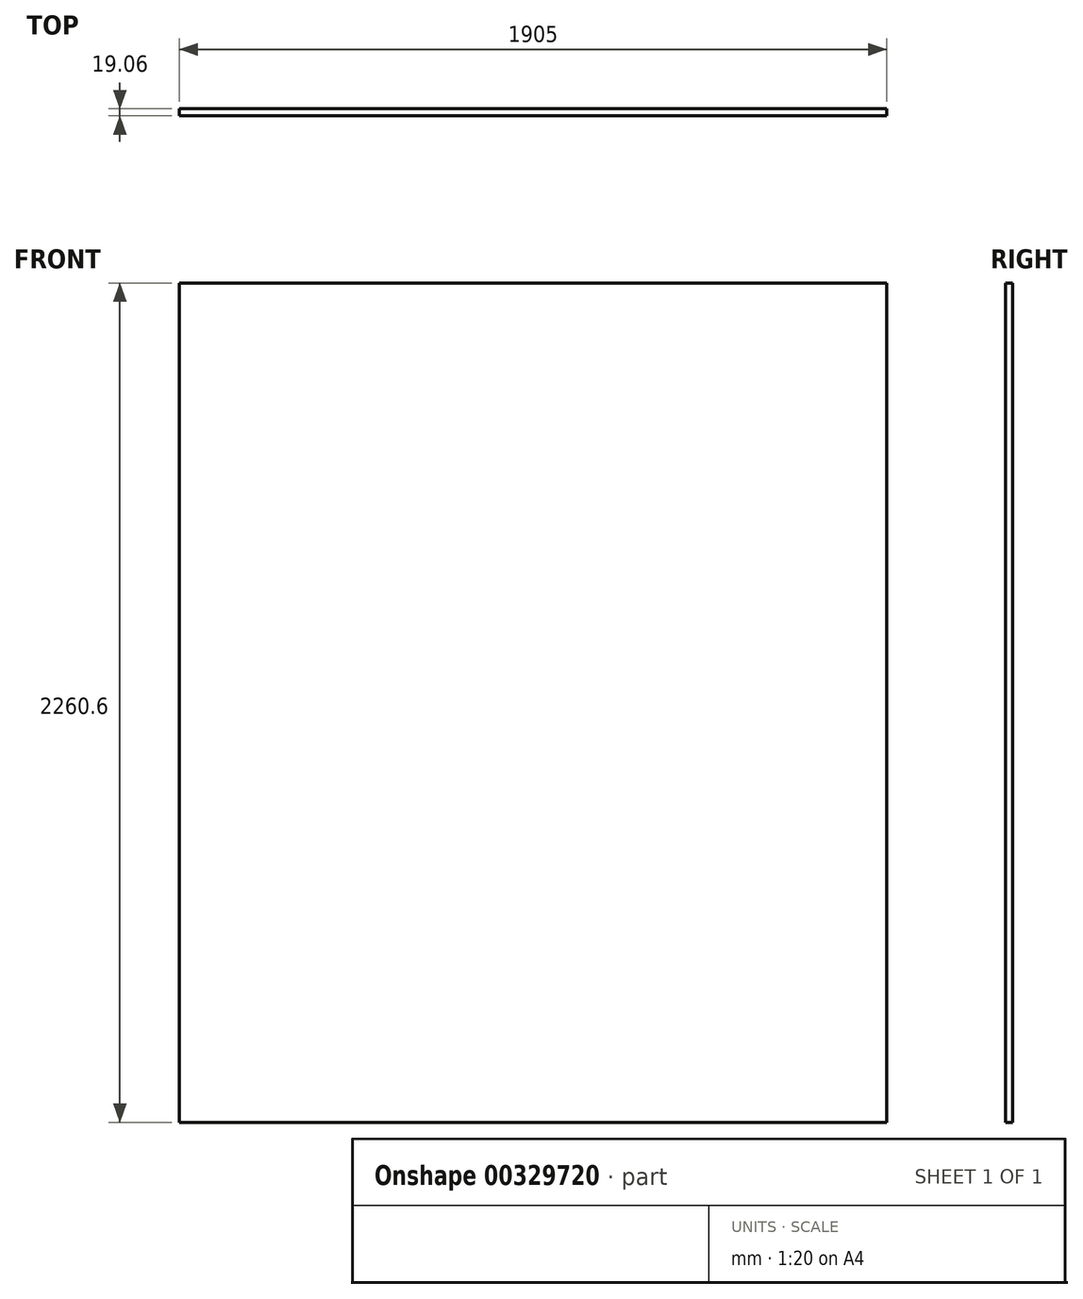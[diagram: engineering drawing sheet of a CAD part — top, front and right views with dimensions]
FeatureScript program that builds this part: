
annotation { "Feature Type Name" : "Feature", "Feature Type Description" : "" }
export const myFeature = defineFeature(function(context is Context, id is Id, definition is map)
    precondition{}
    {
        {
            var Q0;
            Q0=qCreatedBy(makeId("Front.planeOp"),FACE);
            var sketch = newSketch(context, id + "F0", { "sketchPlane" : qUnion([Q0])});
            skLineSegment(sketch, "E0.bottom", {"start": v(-952.5, 1130.3) * mm, "end": v(952.5, 1130.3) * mm});
            skLineSegment(sketch, "E0.top", {"start": v(-952.5, -1130.3) * mm, "end": v(952.5, -1130.3) * mm});
            skLineSegment(sketch, "E0.left", {"start": v(-952.5, 1130.3) * mm, "end": v(-952.5, -1130.3) * mm});
            skLineSegment(sketch, "E0.right", {"start": v(952.5, 1130.3) * mm, "end": v(952.5, -1130.3) * mm});
            skPoint(sketch, "E0.middle", {"position": v(0, 0) * mm});
            skSolve(sketch);
        }
        {
            var Q0;
            Q0=makeQuery(id+"F0.imprint","IMPRINT",FACE,{"disambiguationData":[TD([[makeQuery(id+"F0.imprint","IMPRINT",EDGE,{"derivedFrom":sQuery(id+"F0.wireOp",EDGE,"E0.bottom")}),-1.0]])]});
            extrude(context, id + "F1", {"entities" : qUnion([Q0]), "endBound" : BoundingType.SYMMETRIC, "depth" : 19.05 * mm});
        }
    });
